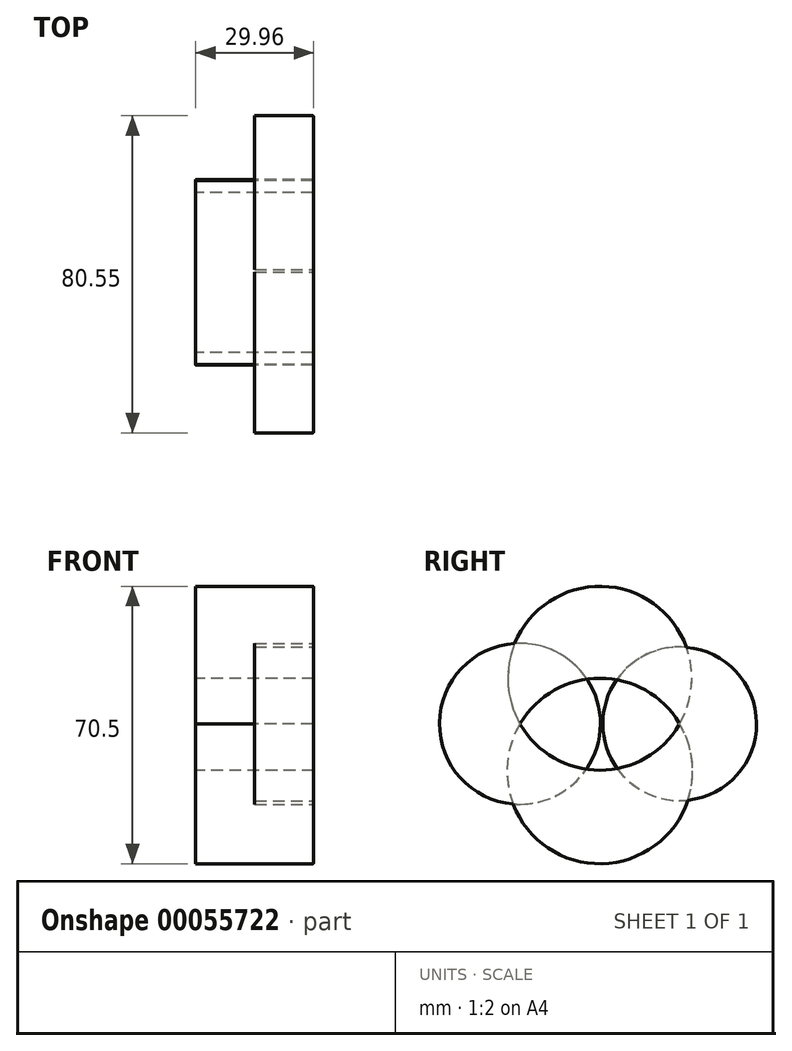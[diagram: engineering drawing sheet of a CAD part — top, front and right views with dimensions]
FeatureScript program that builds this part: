
annotation { "Feature Type Name" : "Feature", "Feature Type Description" : "" }
export const myFeature = defineFeature(function(context is Context, id is Id, definition is map)
    precondition{}
    {
        {
            var Q0;
            Q0=qCreatedBy(makeId("Right.planeOp"),FACE);
            var sketch = newSketch(context, id + "F0", { "sketchPlane" : qUnion([Q0])});
            skCircle(sketch, "E0", {"center": v(0, 0) * mm, "radius": 23.57 * mm});
            skCircle(sketch, "E1", {"center": v(0, 23.57) * mm, "radius": 23.36 * mm});
            skSolve(sketch);
        }
        {
            var Q0;
            {var subQ0=sQuery(id+"F0.wireOp",EDGE,"E1");var subQ1=sQuery(id+"F0.wireOp",EDGE,"E0");var subQ2=makeQuery(id+"F0.imprint","INTERSECT",VERTEX,{"disambiguationData":[OD(0.0)],"derivedFrom":[subQ1,subQ0]});Q0=makeQuery(id+"F0.imprint","IMPRINT",FACE,{"disambiguationData":[TD([[makeQuery(id+"F0.imprint","IMPRINT",EDGE,{"disambiguationData":[TD([[subQ2,1.0]])],"derivedFrom":subQ1}),-1.0]])]});}
            var Q1;
            {var subQ0=sQuery(id+"F0.wireOp",EDGE,"E1");var subQ1=sQuery(id+"F0.wireOp",EDGE,"E0");var subQ2=makeQuery(id+"F0.imprint","INTERSECT",VERTEX,{"disambiguationData":[OD(0.0)],"derivedFrom":[subQ1,subQ0]});Q1=makeQuery(id+"F0.imprint","IMPRINT",FACE,{"disambiguationData":[TD([[makeQuery(id+"F0.imprint","IMPRINT",EDGE,{"disambiguationData":[TD([[subQ2,-1.0]])],"derivedFrom":subQ1}),1.0]])]});}
            extrude(context, id + "F1", {"entities" : qUnion([Q0, Q1]), "depth" : 29.96 * mm});
        }
        {
            var Q0;
            {var subQ0=sQuery(id+"F0.wireOp",EDGE,"E1");var subQ1=sQuery(id+"F0.wireOp",EDGE,"E0");var subQ2=makeQuery(id+"F0.imprint","INTERSECT",VERTEX,{"disambiguationData":[OD(0.0)],"derivedFrom":[subQ1,subQ0]});Q0=makeQuery(id+"F1.opExtrude","CAP_FACE",FACE,{"disambiguationData":[OSD([subQ1,subQ0]),TDD([makeQuery(id+"F0.imprint","IMPRINT",EDGE,{"disambiguationData":[TD([[subQ2,-1.0]])],"derivedFrom":subQ1}),makeQuery(id+"F0.imprint","IMPRINT",EDGE,{"disambiguationData":[TD([[subQ2,-1.0]])],"derivedFrom":subQ0})])],"isStart":false});}
            var sketch = newSketch(context, id + "F2", { "sketchPlane" : qUnion([Q0])});
            skLineSegment(sketch, "E2.bottom", {"start": v(0, 0) * mm, "end": v(0, 0) * mm});
            skLineSegment(sketch, "E2.top", {"start": v(0, 23.57) * mm, "end": v(0, 23.57) * mm});
            skLineSegment(sketch, "E2.left", {"start": v(0, 0) * mm, "end": v(0, 23.57) * mm});
            skLineSegment(sketch, "E2.right", {"start": v(0, 0) * mm, "end": v(0, 23.57) * mm});
            skCircle(sketch, "E3", {"center": v(-20.3, 12) * mm, "radius": 20.44 * mm});
            skCircle(sketch, "E4", {"center": v(20.3, 12) * mm, "radius": 19.53 * mm});
            skSolve(sketch);
        }
        {
            var Q0;
            Q0 = qSketchRegion(id + "F2", true);
            extrude(context, id + "F3", {"entities" : qUnion([Q0]), "oppositeDirection" : true, "depth" : 14.95 * mm});
        }
        {
            var Q0;
            Q0=makeQuery(id+"F3.opExtrude","CAP_EDGE",EDGE,{"disambiguationData":[OSD([sQuery(id+"F2.wireOp",EDGE,"E3")])],"isStart":true});
            var Q1;
            Q1=makeQuery(id+"F3.opExtrude","CAP_EDGE",EDGE,{"disambiguationData":[OSD([sQuery(id+"F2.wireOp",EDGE,"E4")])],"isStart":true});
            var Q2;
            {var subQ0=sQuery(id+"F0.wireOp",EDGE,"E1");var subQ1=sQuery(id+"F0.wireOp",EDGE,"E0");Q2=makeQuery(id+"F1.opExtrude","CAP_EDGE",EDGE,{"disambiguationData":[OSD([subQ0]),TDD([makeQuery(id+"F0.imprint","IMPRINT",EDGE,{"disambiguationData":[TD([[makeQuery(id+"F0.imprint","INTERSECT",VERTEX,{"disambiguationData":[OD(0.0)],"derivedFrom":[subQ1,subQ0]}),1.0]])],"derivedFrom":subQ0})])],"isStart":false});}
            var Q3;
            {var subQ0=sQuery(id+"F0.wireOp",EDGE,"E1");var subQ1=sQuery(id+"F0.wireOp",EDGE,"E0");Q3=makeQuery(id+"F1.opExtrude","CAP_EDGE",EDGE,{"disambiguationData":[OSD([subQ1]),TDD([makeQuery(id+"F0.imprint","IMPRINT",EDGE,{"disambiguationData":[TD([[makeQuery(id+"F0.imprint","INTERSECT",VERTEX,{"disambiguationData":[OD(0.0)],"derivedFrom":[subQ1,subQ0]}),-1.0]])],"derivedFrom":subQ1})])],"isStart":false});}
            fillet(context, id + "F4", {"entities" : qUnion([Q0, Q1, Q2, Q3]), "radius" : 0.24 * mm, "tangentPropagation" : true, "allowEdgeOverflow" : false});
        }
        {
            var Q0;
            {var subQ0=sQuery(id+"F0.wireOp",EDGE,"E1");var subQ1=sQuery(id+"F0.wireOp",EDGE,"E0");var subQ2=makeQuery(id+"F0.imprint","INTERSECT",VERTEX,{"disambiguationData":[OD(0.0)],"derivedFrom":[subQ1,subQ0]});var subQ4=makeQuery(id+"F0.imprint","IMPRINT",EDGE,{"disambiguationData":[TD([[subQ2,1.0]])],"derivedFrom":subQ0});Q0=makeQuery(id+"F4.opFillet","BLEND_EDGE",EDGE,{"blendedFrom":[makeQuery(id+"F1.opExtrude","CAP_EDGE",EDGE,{"disambiguationData":[OSD([subQ0]),TDD([subQ4])],"isStart":false}),makeQuery(id+"F1.opExtrude","CAP_FACE",FACE,{"disambiguationData":[OSD([subQ1,subQ0]),TDD([makeQuery(id+"F0.imprint","IMPRINT",EDGE,{"disambiguationData":[TD([[subQ2,1.0]])],"derivedFrom":subQ1}),subQ4])],"isStart":false})],"blendedInto":[makeQuery(id+"F1.opExtrude","CAP_FACE",FACE,{"disambiguationData":[OSD([subQ1,subQ0]),TDD([makeQuery(id+"F0.imprint","IMPRINT",EDGE,{"disambiguationData":[TD([[subQ2,1.0]])],"derivedFrom":subQ1}),subQ4])],"isStart":false})]});}
            var Q1;
            {var subQ0=sQuery(id+"F2.wireOp",EDGE,"E3");Q1=makeQuery(id+"F4.opFillet","BLEND_EDGE",EDGE,{"blendedFrom":[makeQuery(id+"F3.opExtrude","CAP_EDGE",EDGE,{"disambiguationData":[OSD([subQ0])],"isStart":true}),makeQuery(id+"F3.opExtrude","CAP_FACE",FACE,{"disambiguationData":[OSD([subQ0])],"isStart":true})],"blendedInto":[makeQuery(id+"F3.opExtrude","CAP_FACE",FACE,{"disambiguationData":[OSD([subQ0])],"isStart":true})]});}
            var Q2;
            {var subQ0=sQuery(id+"F2.wireOp",EDGE,"E4");Q2=makeQuery(id+"F4.opFillet","BLEND_EDGE",EDGE,{"blendedFrom":[makeQuery(id+"F3.opExtrude","CAP_EDGE",EDGE,{"disambiguationData":[OSD([subQ0])],"isStart":true}),makeQuery(id+"F3.opExtrude","SWEPT_FACE",FACE,{"disambiguationData":[OSD([subQ0])]})],"blendedInto":[makeQuery(id+"F3.opExtrude","SWEPT_FACE",FACE,{"disambiguationData":[OSD([subQ0])]})]});}
            var Q3;
            {var subQ0=sQuery(id+"F0.wireOp",EDGE,"E1");var subQ1=sQuery(id+"F0.wireOp",EDGE,"E0");var subQ2=makeQuery(id+"F0.imprint","INTERSECT",VERTEX,{"disambiguationData":[OD(0.0)],"derivedFrom":[subQ1,subQ0]});Q3=makeQuery(id+"F1.opExtrude","CAP_FACE",FACE,{"disambiguationData":[OSD([subQ1,subQ0]),TDD([makeQuery(id+"F0.imprint","IMPRINT",EDGE,{"disambiguationData":[TD([[subQ2,-1.0]])],"derivedFrom":subQ1}),makeQuery(id+"F0.imprint","IMPRINT",EDGE,{"disambiguationData":[TD([[subQ2,-1.0]])],"derivedFrom":subQ0})])],"isStart":false});}
            var Q4;
            {var subQ0=sQuery(id+"F0.wireOp",EDGE,"E1");var subQ1=sQuery(id+"F0.wireOp",EDGE,"E0");var subQ2=makeQuery(id+"F0.imprint","INTERSECT",VERTEX,{"disambiguationData":[OD(0.0)],"derivedFrom":[subQ1,subQ0]});var subQ4=makeQuery(id+"F0.imprint","IMPRINT",EDGE,{"disambiguationData":[TD([[subQ2,-1.0]])],"derivedFrom":subQ1});Q4=makeQuery(id+"F4.opFillet","BLEND_EDGE",EDGE,{"blendedFrom":[makeQuery(id+"F1.opExtrude","CAP_EDGE",EDGE,{"disambiguationData":[OSD([subQ1]),TDD([subQ4])],"isStart":false}),makeQuery(id+"F1.opExtrude","CAP_FACE",FACE,{"disambiguationData":[OSD([subQ1,subQ0]),TDD([subQ4,makeQuery(id+"F0.imprint","IMPRINT",EDGE,{"disambiguationData":[TD([[subQ2,-1.0]])],"derivedFrom":subQ0})])],"isStart":false})],"blendedInto":[makeQuery(id+"F1.opExtrude","CAP_FACE",FACE,{"disambiguationData":[OSD([subQ1,subQ0]),TDD([subQ4,makeQuery(id+"F0.imprint","IMPRINT",EDGE,{"disambiguationData":[TD([[subQ2,-1.0]])],"derivedFrom":subQ0})])],"isStart":false})]});}
            var Q5;
            {var subQ0=sQuery(id+"F0.wireOp",EDGE,"E1");var subQ1=sQuery(id+"F0.wireOp",EDGE,"E0");Q5=makeQuery(id+"F1.opExtrude","CAP_EDGE",EDGE,{"disambiguationData":[OSD([subQ1]),TDD([makeQuery(id+"F0.imprint","IMPRINT",EDGE,{"disambiguationData":[TD([[makeQuery(id+"F0.imprint","INTERSECT",VERTEX,{"disambiguationData":[OD(0.0)],"derivedFrom":[subQ1,subQ0]}),1.0]])],"derivedFrom":subQ1})])],"isStart":false});}
            fillet(context, id + "F5", {"entities" : qUnion([Q0, Q1, Q2, Q3, Q4, Q5]), "radius" : 93.17 * mm, "tangentPropagation" : true, "allowEdgeOverflow" : false});
        }
    });
